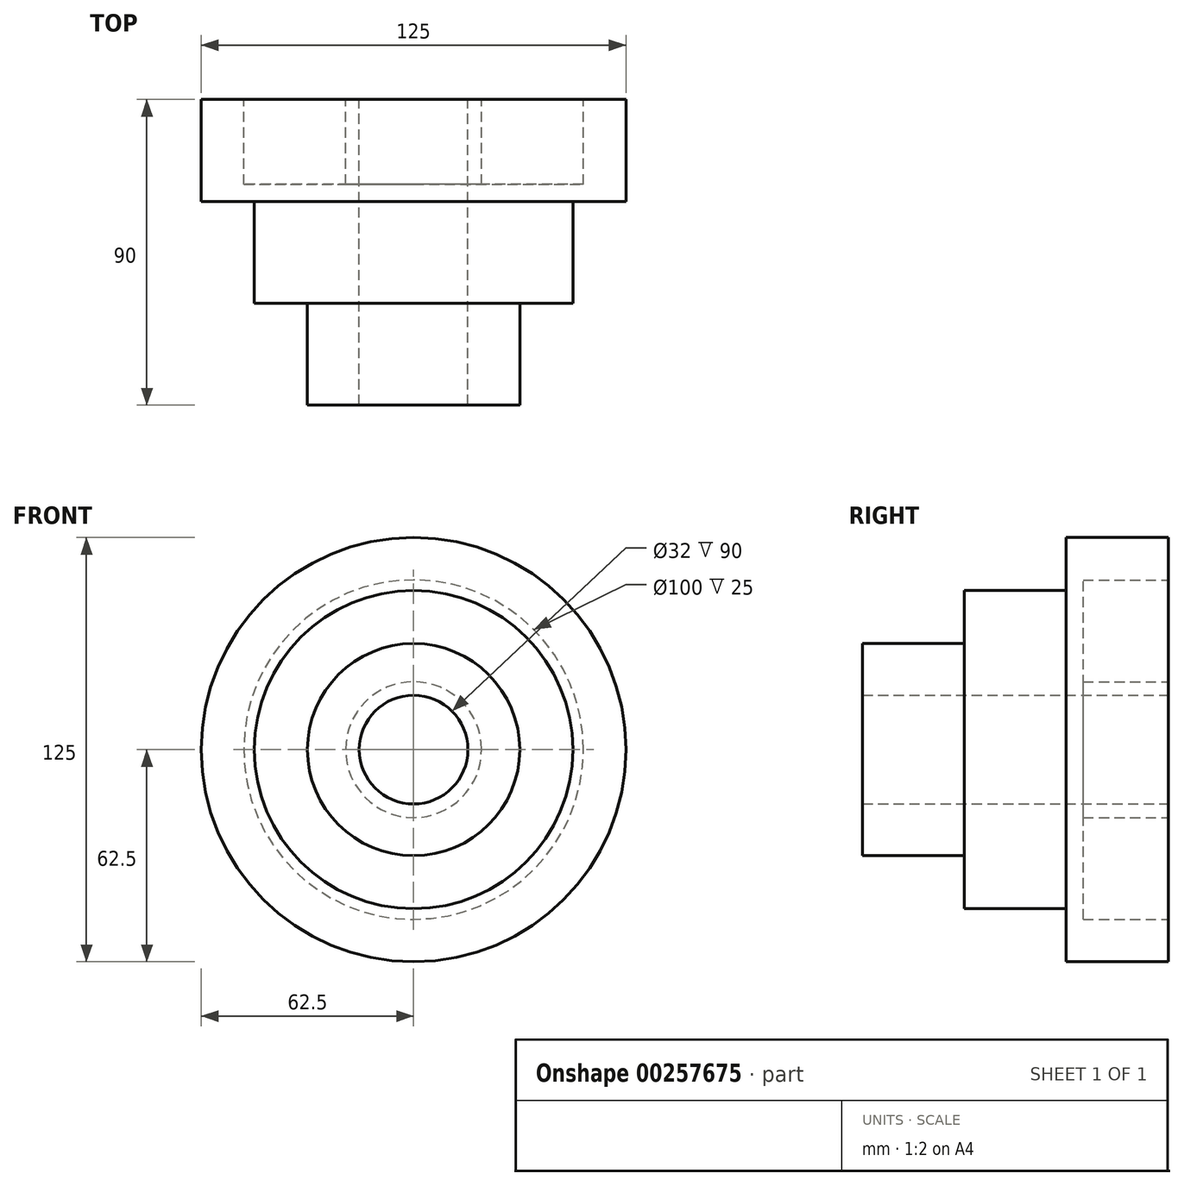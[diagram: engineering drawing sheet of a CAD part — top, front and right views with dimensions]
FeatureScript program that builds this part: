
annotation { "Feature Type Name" : "Feature", "Feature Type Description" : "" }
export const myFeature = defineFeature(function(context is Context, id is Id, definition is map)
    precondition{}
    {
        {
            var Q0;
            Q0=qCreatedBy(makeId("Front.planeOp"),FACE);
            var sketch = newSketch(context, id + "F0", { "sketchPlane" : qUnion([Q0])});
            skCircle(sketch, "E0", {"center": v(0, 0) * mm, "radius": 62.5 * mm});
            skCircle(sketch, "E1", {"center": v(0, 0) * mm, "radius": 31.25 * mm});
            skCircle(sketch, "E2", {"center": v(0, 0) * mm, "radius": 46.88 * mm});
            skCircle(sketch, "E3", {"center": v(0, 0) * mm, "radius": 16 * mm});
            skSolve(sketch);
        }
        {
            var Q0;
            Q0=makeQuery(id+"F0.imprint","IMPRINT",FACE,{"disambiguationData":[TD([[makeQuery(id+"F0.imprint","IMPRINT",EDGE,{"derivedFrom":sQuery(id+"F0.wireOp",EDGE,"E1")}),1.0]])]});
            extrude(context, id + "F1", {"entities" : qUnion([Q0]), "depth" : 90 * mm});
        }
        {
            var Q0;
            Q0=makeQuery(id+"F0.imprint","IMPRINT",FACE,{"disambiguationData":[TD([[makeQuery(id+"F0.imprint","IMPRINT",EDGE,{"derivedFrom":sQuery(id+"F0.wireOp",EDGE,"E1")}),-1.0]])]});
            extrude(context, id + "F2", {"entities" : qUnion([Q0]), "operationType" : NewBodyOperationType.ADD, "depth" : 60 * mm});
        }
        {
            var Q0;
            Q0=makeQuery(id+"F0.imprint","IMPRINT",FACE,{"disambiguationData":[TD([[makeQuery(id+"F0.imprint","IMPRINT",EDGE,{"derivedFrom":sQuery(id+"F0.wireOp",EDGE,"E0")}),1.0]])]});
            extrude(context, id + "F3", {"entities" : qUnion([Q0]), "operationType" : NewBodyOperationType.ADD, "depth" : 30 * mm});
        }
        {
            var Q0;
            Q0=qCreatedBy(makeId("Front.planeOp"),FACE);
            var sketch = newSketch(context, id + "F4", { "sketchPlane" : qUnion([Q0])});
            skCircle(sketch, "E4", {"center": v(0, 0) * mm, "radius": 20 * mm});
            skCircle(sketch, "E5", {"center": v(0, 0) * mm, "radius": 50 * mm});
            skSolve(sketch);
        }
        {
            var Q0;
            Q0 = qSketchRegion(id + "F4", true);
            extrude(context, id + "F5", {"entities" : qUnion([Q0]), "operationType" : NewBodyOperationType.REMOVE, "depth" : 25 * mm});
        }
    });
